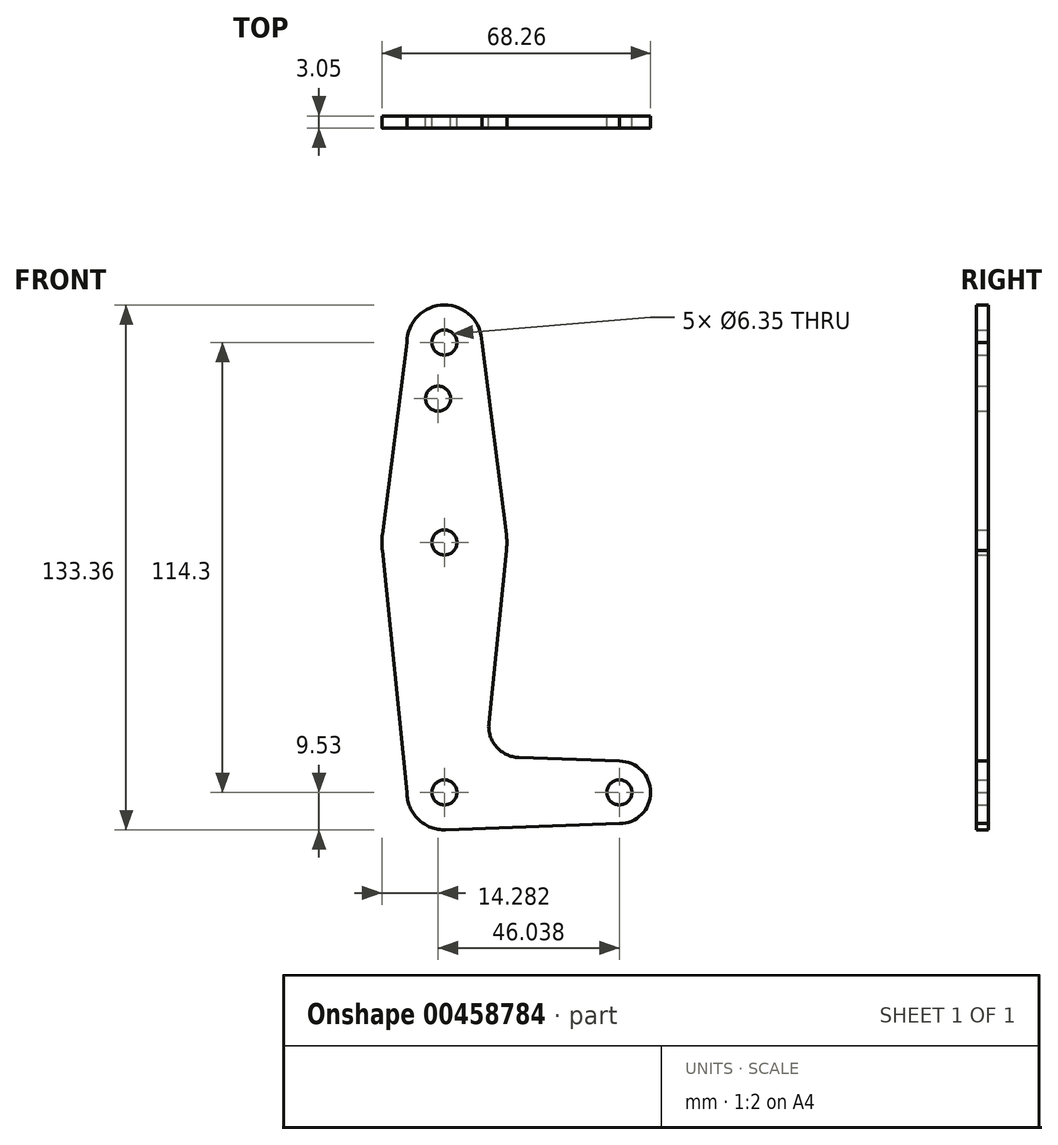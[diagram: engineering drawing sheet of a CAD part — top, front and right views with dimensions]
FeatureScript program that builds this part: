
annotation { "Feature Type Name" : "Feature", "Feature Type Description" : "" }
export const myFeature = defineFeature(function(context is Context, id is Id, definition is map)
    precondition{}
    {
        {
            var Q0;
            Q0=qCreatedBy(makeId("Front.planeOp"),FACE);
            var sketch = newSketch(context, id + "F0", { "sketchPlane" : qUnion([Q0])});
            skCircle(sketch, "E0", {"center": v(0, 63.5) * mm, "radius": 15.88 * mm});
            skCircle(sketch, "E1", {"center": v(0, 114.3) * mm, "radius": 9.53 * mm});
            skCircle(sketch, "E2", {"center": v(0, 0) * mm, "radius": 9.53 * mm});
            skCircle(sketch, "E3", {"center": v(44.45, 0) * mm, "radius": 7.94 * mm});
            skLineSegment(sketch, "E4", {"start": v(0, 0) * mm, "end": v(44.45, 0) * mm});
            skCircle(sketch, "E5", {"center": v(-1.59, 100.03) * mm, "radius": 3.18 * mm});
            skCircle(sketch, "E6", {"center": v(0, 114.3) * mm, "radius": 3.18 * mm});
            skCircle(sketch, "E7", {"center": v(0, 63.5) * mm, "radius": 3.18 * mm});
            skCircle(sketch, "E8", {"center": v(0, 0) * mm, "radius": 3.18 * mm});
            skCircle(sketch, "E9", {"center": v(44.45, 0) * mm, "radius": 3.18 * mm});
            skLineSegment(sketch, "E10", {"start": v(-9.53, 114.3) * mm, "end": v(-15.75, 65.5) * mm});
            skLineSegment(sketch, "E11", {"start": v(9.53, 114.3) * mm, "end": v(15.75, 65.5) * mm});
            skLineSegment(sketch, "E12", {"start": v(-9.53, 0) * mm, "end": v(-15.75, 61.5) * mm});
            skLineSegment(sketch, "E13", {"start": v(11.3, 17.6) * mm, "end": v(15.75, 61.5) * mm});
            skLineSegment(sketch, "E14", {"start": v(44.45, 7.94) * mm, "end": v(18.93, 8.85) * mm});
            skLineSegment(sketch, "E15", {"start": v(44.45, -7.94) * mm, "end": v(0, -9.53) * mm});
            skPoint(sketch, "E16.newPointB", {"position": v(0, 9.53) * mm});
            skArc(sketch, "E16.filletArc", {"start": v(11.3, 17.6) * mm, "mid": v(13.22, 11.57) * mm, "end": v(18.93, 8.85) * mm});
            skLineSegment(sketch, "E17", {"start": v(0, 114.3) * mm, "end": v(0, 63.5) * mm, "construction": true});
            skSolve(sketch);
        }
        {
            var Q0;
            Q0 = qSketchRegion(id + "F0", true);
            extrude(context, id + "F1", {"entities" : qUnion([Q0]), "depth" : 3.05 * mm});
        }
    });
